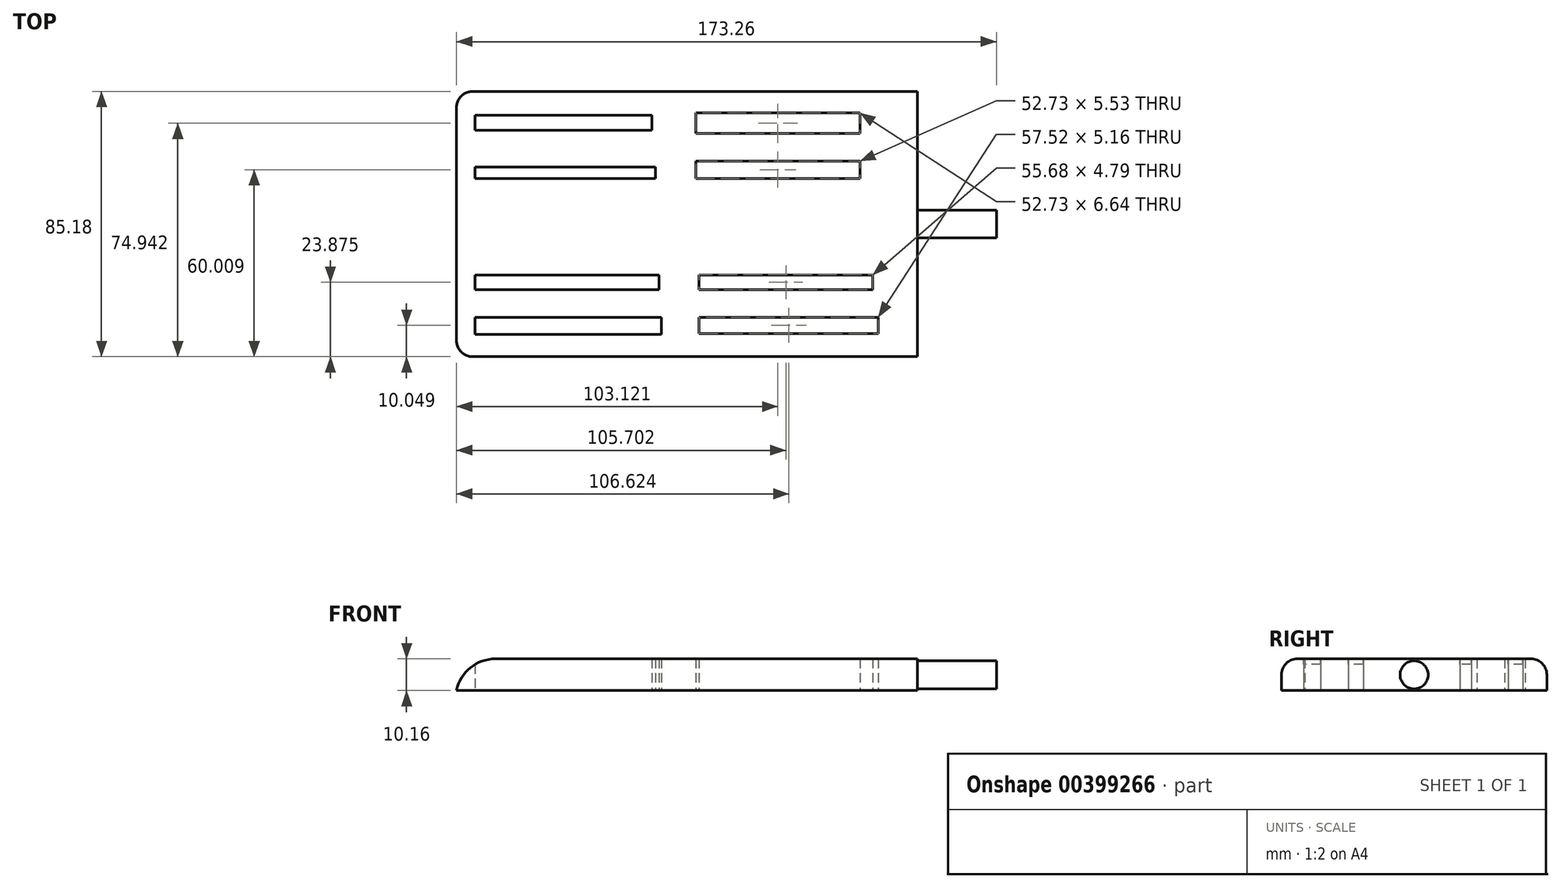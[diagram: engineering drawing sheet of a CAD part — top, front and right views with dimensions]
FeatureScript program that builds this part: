
annotation { "Feature Type Name" : "Feature", "Feature Type Description" : "" }
export const myFeature = defineFeature(function(context is Context, id is Id, definition is map)
    precondition{}
    {
        {
            var Q0;
            Q0=qCreatedBy(makeId("Top.planeOp"),FACE);
            var sketch = newSketch(context, id + "F0", { "sketchPlane" : qUnion([Q0])});
            skLineSegment(sketch, "E0.bottom", {"start": v(-73.93, 42.59) * mm, "end": v(73.93, 42.59) * mm});
            skLineSegment(sketch, "E0.top", {"start": v(-73.93, -42.59) * mm, "end": v(73.93, -42.59) * mm});
            skLineSegment(sketch, "E0.left", {"start": v(-73.93, 42.59) * mm, "end": v(-73.93, -42.59) * mm});
            skLineSegment(sketch, "E0.right", {"start": v(73.93, 42.59) * mm, "end": v(73.93, -42.59) * mm});
            skPoint(sketch, "E0.middle", {"position": v(0, 0) * mm});
            skLineSegment(sketch, "E1.bottom", {"start": v(-67.96, 34.93) * mm, "end": v(-11.18, 34.93) * mm});
            skLineSegment(sketch, "E1.top", {"start": v(-67.96, 30.14) * mm, "end": v(-11.18, 30.14) * mm});
            skLineSegment(sketch, "E1.left", {"start": v(-67.96, 34.93) * mm, "end": v(-67.96, 30.14) * mm});
            skLineSegment(sketch, "E1.right", {"start": v(-11.18, 34.93) * mm, "end": v(-11.18, 30.14) * mm});
            skLineSegment(sketch, "E2.bottom", {"start": v(2.83, 35.67) * mm, "end": v(55.55, 35.67) * mm});
            skLineSegment(sketch, "E2.top", {"start": v(2.83, 29.03) * mm, "end": v(55.55, 29.03) * mm});
            skLineSegment(sketch, "E2.left", {"start": v(2.83, 35.67) * mm, "end": v(2.83, 29.03) * mm});
            skLineSegment(sketch, "E2.right", {"start": v(55.55, 35.67) * mm, "end": v(55.55, 29.03) * mm});
            skLineSegment(sketch, "E3.bottom", {"start": v(-67.96, 18.34) * mm, "end": v(-10.08, 18.34) * mm});
            skLineSegment(sketch, "E3.top", {"start": v(-67.96, 14.65) * mm, "end": v(-10.08, 14.65) * mm});
            skLineSegment(sketch, "E3.left", {"start": v(-67.96, 18.34) * mm, "end": v(-67.96, 14.65) * mm});
            skLineSegment(sketch, "E3.right", {"start": v(-10.08, 18.34) * mm, "end": v(-10.08, 14.65) * mm});
            skLineSegment(sketch, "E4.bottom", {"start": v(2.83, 14.65) * mm, "end": v(55.55, 14.65) * mm});
            skLineSegment(sketch, "E4.top", {"start": v(2.83, 20.18) * mm, "end": v(55.55, 20.18) * mm});
            skLineSegment(sketch, "E4.left", {"start": v(2.83, 14.65) * mm, "end": v(2.83, 20.18) * mm});
            skLineSegment(sketch, "E4.right", {"start": v(55.55, 14.65) * mm, "end": v(55.55, 20.18) * mm});
            skLineSegment(sketch, "E5.bottom", {"start": v(-67.96, -16.32) * mm, "end": v(-8.97, -16.32) * mm});
            skLineSegment(sketch, "E5.top", {"start": v(-67.96, -21.11) * mm, "end": v(-8.97, -21.11) * mm});
            skLineSegment(sketch, "E5.left", {"start": v(-67.96, -16.32) * mm, "end": v(-67.96, -21.11) * mm});
            skLineSegment(sketch, "E5.right", {"start": v(-8.97, -16.32) * mm, "end": v(-8.97, -21.11) * mm});
            skLineSegment(sketch, "E6.bottom", {"start": v(-67.96, -29.96) * mm, "end": v(-8.23, -29.96) * mm});
            skLineSegment(sketch, "E6.top", {"start": v(-67.96, -35.5) * mm, "end": v(-8.23, -35.5) * mm});
            skLineSegment(sketch, "E6.left", {"start": v(-67.96, -29.96) * mm, "end": v(-67.96, -35.5) * mm});
            skLineSegment(sketch, "E6.right", {"start": v(-8.23, -29.96) * mm, "end": v(-8.23, -35.5) * mm});
            skLineSegment(sketch, "E7.bottom", {"start": v(3.93, -16.32) * mm, "end": v(59.6, -16.32) * mm});
            skLineSegment(sketch, "E7.top", {"start": v(3.93, -21.11) * mm, "end": v(59.6, -21.11) * mm});
            skLineSegment(sketch, "E7.left", {"start": v(3.93, -16.32) * mm, "end": v(3.93, -21.11) * mm});
            skLineSegment(sketch, "E7.right", {"start": v(59.6, -16.32) * mm, "end": v(59.6, -21.11) * mm});
            skLineSegment(sketch, "E8.bottom", {"start": v(3.93, -29.96) * mm, "end": v(61.45, -29.96) * mm});
            skLineSegment(sketch, "E8.top", {"start": v(3.93, -35.12) * mm, "end": v(61.45, -35.12) * mm});
            skLineSegment(sketch, "E8.left", {"start": v(3.93, -29.96) * mm, "end": v(3.93, -35.12) * mm});
            skLineSegment(sketch, "E8.right", {"start": v(61.45, -29.96) * mm, "end": v(61.45, -35.12) * mm});
            skSolve(sketch);
        }
        {
            var Q0;
            Q0=makeQuery(id+"F0.imprint","IMPRINT",FACE,{"disambiguationData":[TD([[makeQuery(id+"F0.imprint","IMPRINT",EDGE,{"derivedFrom":sQuery(id+"F0.wireOp",EDGE,"E0.bottom")}),-1.0]])]});
            extrude(context, id + "F1", {"entities" : qUnion([Q0]), "depth" : 10.16 * mm});
        }
        {
            var Q0;
            Q0=makeQuery(id+"F1.opExtrude","CAP_EDGE",EDGE,{"disambiguationData":[OSD([sQuery(id+"F0.wireOp",EDGE,"E0.left")])],"isStart":false});
            fillet(context, id + "F2", {"entities" : qUnion([Q0]), "radius" : 12.7 * mm, "tangentPropagation" : true, "allowEdgeOverflow" : false});
        }
        {
            var Q0;
            Q0=makeQuery(id+"F1.opExtrude","CAP_EDGE",EDGE,{"disambiguationData":[OSD([sQuery(id+"F0.wireOp",EDGE,"E0.top")])],"isStart":false});
            var Q1;
            Q1=makeQuery(id+"F1.opExtrude","CAP_EDGE",EDGE,{"disambiguationData":[OSD([sQuery(id+"F0.wireOp",EDGE,"E0.bottom")])],"isStart":false});
            fillet(context, id + "F3", {"entities" : qUnion([Q0, Q1]), "radius" : 5.08 * mm, "tangentPropagation" : true, "allowEdgeOverflow" : false});
        }
        {
            var Q0;
            Q0=makeQuery(id+"F1.opExtrude","SWEPT_FACE",FACE,{"disambiguationData":[OSD([sQuery(id+"F0.wireOp",EDGE,"E0.right")])]});
            var sketch = newSketch(context, id + "F4", { "sketchPlane" : qUnion([Q0])});
            skCircle(sketch, "E9", {"center": v(0, 5.03) * mm, "radius": 4.5 * mm});
            skSolve(sketch);
        }
        {
            var Q0;
            Q0=makeQuery(id+"F4.imprint","IMPRINT",FACE,{"disambiguationData":[TD([[makeQuery(id+"F4.imprint","IMPRINT",EDGE,{"derivedFrom":sQuery(id+"F4.wireOp",EDGE,"E9")}),1.0]])]});
            extrude(context, id + "F5", {"entities" : qUnion([Q0]), "operationType" : NewBodyOperationType.ADD, "depth" : 25.4 * mm});
        }
    });
